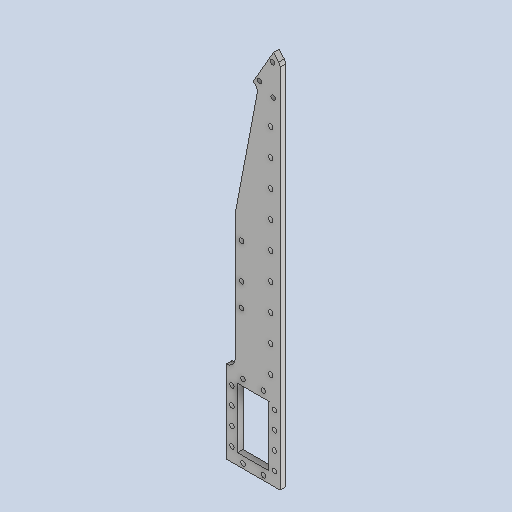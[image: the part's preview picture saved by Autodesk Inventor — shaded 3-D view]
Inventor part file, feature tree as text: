
AUTODESK INVENTOR PART (.ipt)
format: ipt  version: 2025.1 (Build 291241000, 241)  size: 158,720 bytes
history: native  units: mm
features: sketch x7, other x3, plane x2
ambient origin geometry x8: Origin, YZ Plane, XZ Plane, XY Plane, X Axis, Y Axis, Z Axis, Center Point
bodies: Volumenkörper1 (feature_tree)
feature tree (12):
  other  "1012.ipt"
  other  "Volumenkörper1::1012.ipt"
  other  "TaggingFeature1"
  sketch  "Skizze1"  dims[d0=10.0mm]
  sketch  "Skizze2"
  sketch  "Skizze3"
  sketch  "Skizze4"
  sketch  "Skizze5"
  sketch  "Skizze6"
  sketch  "Skizze8"
  plane  "Arbeitsebene1"
  plane  "Arbeitsebene2"
